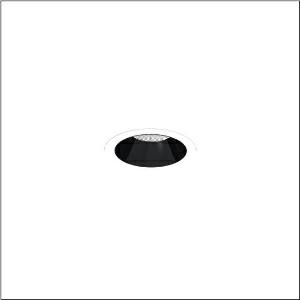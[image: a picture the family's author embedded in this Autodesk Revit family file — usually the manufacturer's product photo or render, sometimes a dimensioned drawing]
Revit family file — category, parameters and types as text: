
# Revit family: lunis_21_m_51db17mc91c
name_source: partatom
category: Lighting Fixtures
units: mm (PartAtom-declared; Revit-internal decimal feet)

## family parameters
Cut with Voids When Loaded = No
Host = Face
Light Source = No
Part Type = Normal
Room Calculation Point = No
Round Connector Dimension = Use Diameter
Shared = No

## types (1)
- --- (1 x LED, 3450 lm, 25.5 W, 4000K)
    Apparent Load = 26 VA
    CIE Flux Codes = 95 100 100 100 100
    Color Rendering = 80
    Color Temperature = 4000K
    Default Elevation = 1800 mm
    Description = Lunis 21,  M, downlight, light control with lens, of PMMA, anti glare with reflector, of PC, light emission: direct distribution, LED rated luminous flux: 1.570lm, light colour: 830/840/865, with terminal, 3-pole, mains connection: 220..240V, AC/DC, 0/50..60Hz, housing, round, of diecast aluminium, traffic white (RAL 9016), diameter: 115mm, clamping range: 1..40mm, protection rating (complete): IP20, protection rating (on room side): IP54, insulation class (complete): insulation class II (safety insulation), certification: CE, impact resistance: IK03, packaging unit: 1 piece
    Height = 0 mm  [stored 0 ft]
    Lamp = 1 x LED
    Lamp Light Flux = 3450 lm
    Lamp Power = 25.5 W
    Lamp count = 1
    Length = 115 mm
    Luminous efficacy = 135 lm/W
    Manufacturer = Siteco
    ModVariant = No
    Model = 51DB17MC91C
    Mounting Place = Ceiling
    Mounting Type = Recessed
    Number of Poles = 1
    OnlyDefault = Yes
    Power Factor = 1
    Product Name = Lunis 21 M
    Product group = downlight
    ProductGroupID = 401
    Protection Class = Protection class II
    Protection Degree = IP 20
    RLX_Detail_Level = 1
    RLX_Emergency_Light_Flux = 0 lm
    RLX_Emergency_Type = 0
    RLX_Emergency_Type_DB = No
    RlxData = <blob elided: 11493 chars, md5=7e72212f>
    Socket = socket
    Standby Power = 0 W
    System Light Flux = 3450 lm
    System Power = 26 W
    Type Comments = individual setting: colour temperature 4000K, luminous flux: 100 % | (ON | ON | OFF | OFF) | 700 mA
    Type Image = l_1290854.jpg
    URL = http://relux.com
    VarID = @adj_026259
    Voltage = 0 V
    Weight = 0.00 kg
    Width = 0 mm  [stored 0 ft]

note: [stored X ft] marks values corroborated as IEEE doubles in the binary element streams (Revit-internal decimal feet)

## geometry (parser evidence)
native form markers: Sweep x10
no freeform markers — native parametric forms only
